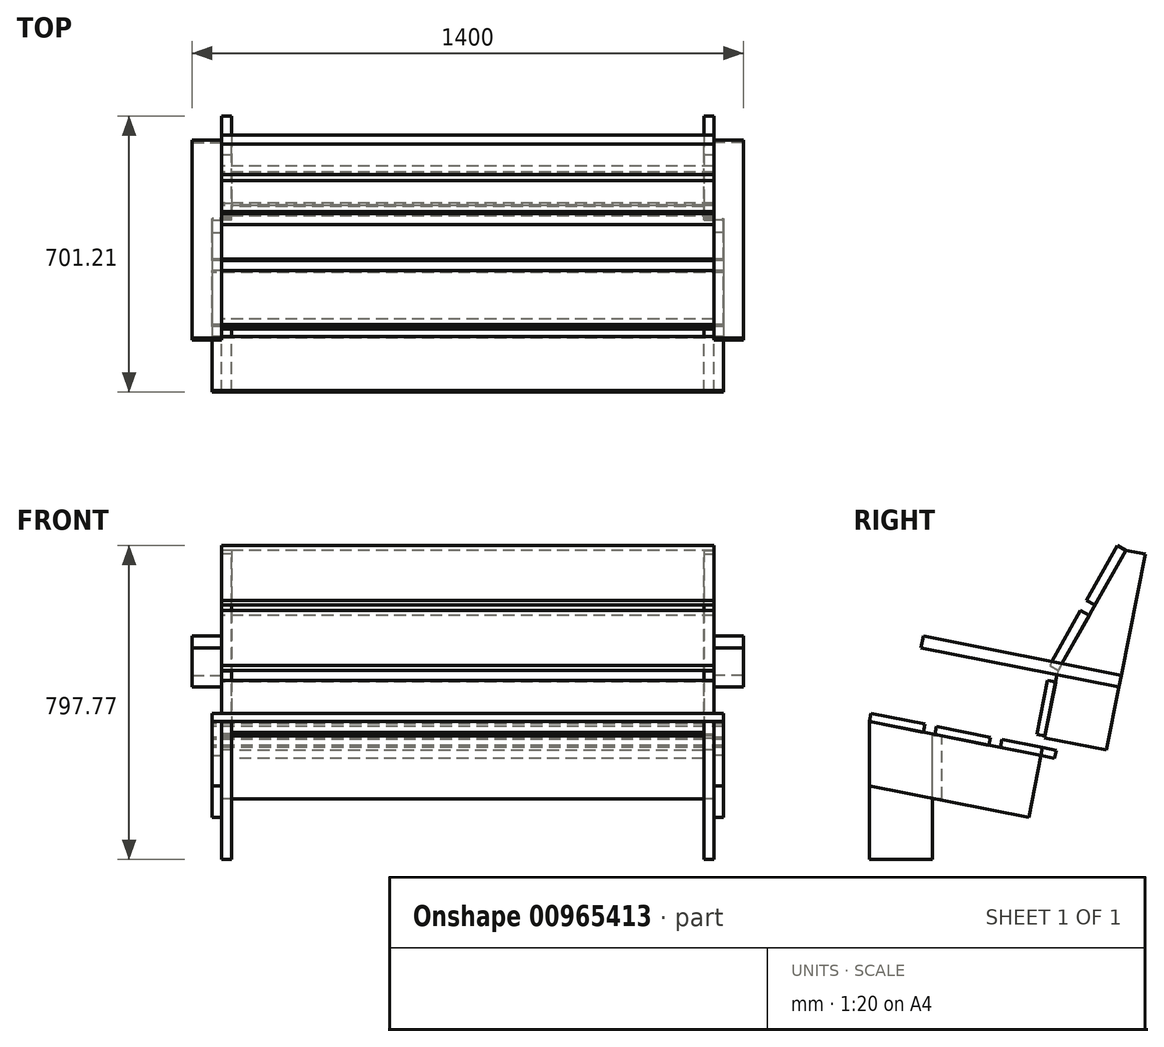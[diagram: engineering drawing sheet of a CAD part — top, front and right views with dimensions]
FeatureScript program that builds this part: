
annotation { "Feature Type Name" : "Feature", "Feature Type Description" : "" }
export const myFeature = defineFeature(function(context is Context, id is Id, definition is map)
    precondition{}
    {
        {
            var Q0;
            Q0=qCreatedBy(makeId("Right.planeOp"),FACE);
            var sketch = newSketch(context, id + "F0", { "sketchPlane" : qUnion([Q0])});
            skPoint(sketch, "E0", {"position": v(-249.54, -686.48) * mm});
            skPoint(sketch, "E1", {"position": v(-237.44, -315.62) * mm});
            skLineSegment(sketch, "E2", {"start": v(-249.54, -686.48) * mm, "end": v(295.32, -698.73) * mm});
            skLineSegment(sketch, "E3", {"start": v(-249.54, -686.48) * mm, "end": v(-249.54, -335.98) * mm});
            skLineSegment(sketch, "E4", {"start": v(295.32, -698.73) * mm, "end": v(451.67, 89.28) * mm});
            skLineSegment(sketch, "E5", {"start": v(451.67, 89.28) * mm, "end": v(402.62, 99) * mm});
            skLineSegment(sketch, "E6", {"start": v(343.93, -453.73) * mm, "end": v(-249.54, -335.98) * mm});
            skLineSegment(sketch, "E7", {"start": v(312.8, -610.67) * mm, "end": v(-249.54, -499.1) * mm});
            skLineSegment(sketch, "E8", {"start": v(229.62, -207.76) * mm, "end": v(132.92, -695.08) * mm});
            skLineSegment(sketch, "E9", {"start": v(-89.54, -690.08) * mm, "end": v(-89.54, -367.73) * mm});
            skLineSegment(sketch, "E10", {"start": v(402.62, 99) * mm, "end": v(229.62, -207.76) * mm});
            skLineSegment(sketch, "E11", {"start": v(390.56, -218.73) * mm, "end": v(-112.01, -119.02) * mm});
            skLineSegment(sketch, "E12", {"start": v(-112.01, -119.02) * mm, "end": v(-117.85, -148.44) * mm});
            skLineSegment(sketch, "E13", {"start": v(-117.85, -148.44) * mm, "end": v(384.72, -248.16) * mm});
            skLineSegment(sketch, "E14", {"start": v(-87.74, -342.6) * mm, "end": v(-92.6, -367.12) * mm});
            skLineSegment(sketch, "E15", {"start": v(-87.74, -342.6) * mm, "end": v(-244.68, -311.46) * mm});
            skLineSegment(sketch, "E16", {"start": v(-249.54, -335.98) * mm, "end": v(-244.68, -311.46) * mm});
            skPoint(sketch, "E17", {"position": v(-43.69, -350.7) * mm});
            skPoint(sketch, "E18", {"position": v(-13.73, -354.7) * mm});
            skLineSegment(sketch, "E19.0", {"start": v(-58.31, -348.44) * mm, "end": v(-63.18, -372.96) * mm});
            skLineSegment(sketch, "E20", {"start": v(-58.31, -348.44) * mm, "end": v(98.63, -379.57) * mm});
            skLineSegment(sketch, "E21", {"start": v(98.63, -379.57) * mm, "end": v(93.76, -404.1) * mm});
            skLineSegment(sketch, "E22.0", {"start": v(128.06, -385.41) * mm, "end": v(123.2, -409.94) * mm});
            skLineSegment(sketch, "E23", {"start": v(128.06, -385.41) * mm, "end": v(285, -416.55) * mm});
            skLineSegment(sketch, "E24", {"start": v(285, -416.55) * mm, "end": v(280.13, -441.07) * mm});
            skLineSegment(sketch, "E25.0", {"start": v(-64.54, -690.08) * mm, "end": v(-64.54, -367.73) * mm});
            skLineSegment(sketch, "E26", {"start": v(402.62, 99) * mm, "end": v(380.85, 111.29) * mm});
            skLineSegment(sketch, "E27", {"start": v(380.85, 111.29) * mm, "end": v(302.25, -28.08) * mm});
            skLineSegment(sketch, "E28", {"start": v(302.25, -28.08) * mm, "end": v(324.03, -40.36) * mm});
            skLineSegment(sketch, "E29.0", {"start": v(287.51, -54.2) * mm, "end": v(309.29, -66.49) * mm});
            skLineSegment(sketch, "E30", {"start": v(287.51, -54.2) * mm, "end": v(208.91, -193.57) * mm});
            skLineSegment(sketch, "E31", {"start": v(208.91, -193.57) * mm, "end": v(230.69, -205.85) * mm});
            skPoint(sketch, "E32.orphan", {"position": v(229.62, -205.25) * mm});
            skLineSegment(sketch, "E33", {"start": v(229.62, -207.76) * mm, "end": v(205.1, -202.89) * mm});
            skLineSegment(sketch, "E34", {"start": v(205.1, -202.89) * mm, "end": v(173.95, -359.83) * mm});
            skLineSegment(sketch, "E35", {"start": v(173.95, -359.83) * mm, "end": v(198.48, -364.7) * mm});
            skSolve(sketch);
        }
        {
            var Q0;
            Q0=qCreatedBy(makeId("Right.planeOp"),FACE);
            var sketch = newSketch(context, id + "F1", { "sketchPlane" : qUnion([Q0])});
            skLineSegment(sketch, "E36.bottom", {"start": v(-245.46, -315.38) * mm, "end": v(-108.13, -342.63) * mm});
            skLineSegment(sketch, "E36.top", {"start": v(-249.54, -335.98) * mm, "end": v(-112.22, -363.23) * mm});
            skLineSegment(sketch, "E36.left", {"start": v(-249.54, -335.98) * mm, "end": v(-245.46, -315.38) * mm});
            skLineSegment(sketch, "E36.right", {"start": v(-112.22, -363.23) * mm, "end": v(-108.13, -342.63) * mm});
            skSolve(sketch);
        }
        {
            var Q0;
            Q0 = qSketchRegion(id + "F1", true);
            extrude(context, id + "F2", {"entities" : qUnion([Q0]), "depth" : 1300 * mm, "offsetDistance" : 25 * mm});
        }
        {
            var Q0;
            Q0=qCreatedBy(makeId("Right.planeOp"),FACE);
            var sketch = newSketch(context, id + "F3", { "sketchPlane" : qUnion([Q0])});
            skLineSegment(sketch, "E37", {"start": v(-82.8, -369.07) * mm, "end": v(54.53, -396.31) * mm});
            skLineSegment(sketch, "E38", {"start": v(-82.8, -369.07) * mm, "end": v(-78.7, -348.47) * mm});
            skLineSegment(sketch, "E39", {"start": v(-78.7, -348.47) * mm, "end": v(58.62, -375.71) * mm});
            skLineSegment(sketch, "E40", {"start": v(54.53, -396.31) * mm, "end": v(58.62, -375.71) * mm});
            skSolve(sketch);
        }
        {
            var Q0;
            Q0 = qSketchRegion(id + "F3", true);
            extrude(context, id + "F4", {"entities" : qUnion([Q0]), "depth" : 1300 * mm, "offsetDistance" : 25 * mm});
        }
        {
            var Q0;
            Q0=qCreatedBy(makeId("Right.planeOp"),FACE);
            var sketch = newSketch(context, id + "F5", { "sketchPlane" : qUnion([Q0])});
            skLineSegment(sketch, "E41.0", {"start": v(88.04, -381.55) * mm, "end": v(83.96, -402.15) * mm});
            skLineSegment(sketch, "E42.0", {"start": v(225.37, -408.8) * mm, "end": v(221.28, -429.4) * mm});
            skLineSegment(sketch, "E43", {"start": v(83.96, -402.15) * mm, "end": v(221.28, -429.4) * mm});
            skLineSegment(sketch, "E44", {"start": v(88.04, -381.55) * mm, "end": v(225.37, -408.8) * mm});
            skSolve(sketch);
        }
        {
            var Q0;
            Q0 = qSketchRegion(id + "F5", true);
            extrude(context, id + "F6", {"entities" : qUnion([Q0]), "depth" : 1300 * mm, "offsetDistance" : 25 * mm});
        }
        {
            var Q0;
            Q0=qCreatedBy(makeId("Right.planeOp"),FACE);
            var sketch = newSketch(context, id + "F7", { "sketchPlane" : qUnion([Q0])});
            skLineSegment(sketch, "E45", {"start": v(224.16, -235.25) * mm, "end": v(196.91, -372.57) * mm});
            skLineSegment(sketch, "E46.0", {"start": v(224.16, -235.25) * mm, "end": v(203.56, -231.16) * mm});
            skLineSegment(sketch, "E47.0", {"start": v(176.32, -368.48) * mm, "end": v(196.91, -372.57) * mm});
            skPoint(sketch, "E48.orphan", {"position": v(205.1, -202.89) * mm});
            skLineSegment(sketch, "E49", {"start": v(203.56, -231.16) * mm, "end": v(176.32, -368.48) * mm});
            skSolve(sketch);
        }
        {
            var Q0;
            Q0 = qSketchRegion(id + "F7", true);
            extrude(context, id + "F8", {"entities" : qUnion([Q0]), "depth" : (1300 - 25) * mm, "offsetDistance" : 25 * mm, "hasSecondDirection" : true, "secondDirectionOppositeDirection" : false, "secondDirectionDepth" : 25 * mm});
        }
        {
            var Q0;
            {var subQ0=sQuery(id+"F0.wireOp",EDGE,"E29.0");Q0=makeQuery(id+"F0.imprint","IMPRINT",FACE,{"disambiguationData":[TD([[makeQuery(id+"F0.imprint","IMPRINT",EDGE,{"derivedFrom":subQ0}),-1.0]])]});}
            var Q1;
            {var subQ0=sQuery(id+"F0.wireOp",EDGE,"E31");Q1=makeQuery(id+"F0.imprint","IMPRINT",FACE,{"disambiguationData":[TD([[makeQuery(id+"F0.imprint","IMPRINT",EDGE,{"derivedFrom":subQ0}),1.0]])]});}
            extrude(context, id + "F9", {"entities" : qUnion([Q0, Q1]), "depth" : (1300 - 25) * mm, "offsetDistance" : 25 * mm, "hasSecondDirection" : true, "secondDirectionOppositeDirection" : false, "secondDirectionDepth" : 25 * mm});
        }
        {
            var Q0;
            {var subQ0=sQuery(id+"F0.wireOp",EDGE,"E26");Q0=makeQuery(id+"F0.imprint","IMPRINT",FACE,{"disambiguationData":[TD([[makeQuery(id+"F0.imprint","IMPRINT",EDGE,{"derivedFrom":subQ0}),1.0]])]});}
            extrude(context, id + "F10", {"entities" : qUnion([Q0]), "depth" : (1300 - 25) * mm, "offsetDistance" : 25 * mm, "hasSecondDirection" : true, "secondDirectionOppositeDirection" : false, "secondDirectionDepth" : 25 * mm});
        }
        {
            var Q0;
            Q0=qCreatedBy(makeId("Right.planeOp"),FACE);
            var sketch = newSketch(context, id + "F11", { "sketchPlane" : qUnion([Q0])});
            skLineSegment(sketch, "E50.0", {"start": v(312.8, -610.67) * mm, "end": v(-249.54, -499.1) * mm});
            skLineSegment(sketch, "E51.0", {"start": v(343.93, -453.73) * mm, "end": v(-249.54, -335.98) * mm});
            skLineSegment(sketch, "E52", {"start": v(343.93, -453.73) * mm, "end": v(312.8, -610.67) * mm});
            skLineSegment(sketch, "E53", {"start": v(-249.54, -335.98) * mm, "end": v(-249.54, -499.1) * mm});
            skSolve(sketch);
        }
        {
            var Q0;
            Q0 = qSketchRegion(id + "F11", true);
            extrude(context, id + "F12", {"entities" : qUnion([Q0]), "depth" : 25 * mm, "offsetDistance" : 25 * mm});
        }
        {
            var Q0;
            Q0=qCreatedBy(makeId("Right.planeOp"),FACE);
            var sketch = newSketch(context, id + "F13", { "sketchPlane" : qUnion([Q0])});
            skLineSegment(sketch, "E54.0", {"start": v(390.56, -218.73) * mm, "end": v(-112.01, -119.02) * mm});
            skLineSegment(sketch, "E55.0", {"start": v(-117.85, -148.44) * mm, "end": v(384.72, -248.16) * mm});
            skLineSegment(sketch, "E56.0", {"start": v(-112.01, -119.02) * mm, "end": v(-117.85, -148.44) * mm});
            skLineSegment(sketch, "E57", {"start": v(390.56, -218.73) * mm, "end": v(384.72, -248.16) * mm});
            skSolve(sketch);
        }
        {
            var Q0;
            Q0 = qSketchRegion(id + "F13", true);
            extrude(context, id + "F14", {"entities" : qUnion([Q0]), "oppositeDirection" : true, "depth" : 50 * mm, "offsetDistance" : 25 * mm, "hasSecondDirection" : true, "secondDirectionOppositeDirection" : false, "secondDirectionDepth" : 25 * mm});
        }
        {
            var Q0;
            Q0=qCreatedBy(makeId("Right.planeOp"),FACE);
            var sketch = newSketch(context, id + "F15", { "sketchPlane" : qUnion([Q0])});
            skLineSegment(sketch, "E58.0", {"start": v(-249.54, -686.48) * mm, "end": v(-249.54, -335.98) * mm});
            skLineSegment(sketch, "E59.0", {"start": v(-89.54, -686.48) * mm, "end": v(-89.54, -367.73) * mm});
            skLineSegment(sketch, "E60", {"start": v(-249.54, -335.98) * mm, "end": v(-89.54, -367.73) * mm});
            skLineSegment(sketch, "E61", {"start": v(-249.54, -686.48) * mm, "end": v(-89.54, -686.48) * mm});
            skPoint(sketch, "E62.orphan", {"position": v(-89.54, -690.08) * mm});
            skSolve(sketch);
        }
        {
            var Q0;
            Q0 = qSketchRegion(id + "F15", true);
            extrude(context, id + "F16", {"entities" : qUnion([Q0]), "depth" : 50 * mm, "offsetDistance" : 25 * mm, "hasSecondDirection" : true, "secondDirectionOppositeDirection" : true, "secondDirectionDepth" : -25 * mm});
        }
        {
            var Q0;
            Q0=qCreatedBy(makeId("Right.planeOp"),FACE);
            var sketch = newSketch(context, id + "F17", { "sketchPlane" : qUnion([Q0])});
            skLineSegment(sketch, "E63.0", {"start": v(297.75, -686.48) * mm, "end": v(451.67, 89.28) * mm});
            skLineSegment(sketch, "E64.0", {"start": v(229.62, -207.76) * mm, "end": v(134.63, -686.48) * mm});
            skLineSegment(sketch, "E65.0", {"start": v(402.62, 99) * mm, "end": v(229.62, -207.76) * mm});
            skLineSegment(sketch, "E66", {"start": v(402.62, 99) * mm, "end": v(451.67, 89.28) * mm});
            skPoint(sketch, "E67.0", {"position": v(-249.54, -686.48) * mm});
            skLineSegment(sketch, "E68", {"start": v(134.63, -686.48) * mm, "end": v(297.75, -686.48) * mm});
            skSolve(sketch);
        }
        {
            var Q0;
            Q0 = qSketchRegion(id + "F17", true);
            extrude(context, id + "F18", {"entities" : qUnion([Q0]), "depth" : 50 * mm, "offsetDistance" : 25 * mm, "hasSecondDirection" : true, "secondDirectionOppositeDirection" : true, "secondDirectionDepth" : -25 * mm});
        }
        {
            var Q0;
            Q0=qCreatedBy(makeId("Right.planeOp"),FACE);
            var sketch = newSketch(context, id + "F19", { "sketchPlane" : qUnion([Q0])});
            skLineSegment(sketch, "E69.0", {"start": v(-64.54, -532.42) * mm, "end": v(-64.54, -372.42) * mm});
            skLineSegment(sketch, "E70.0", {"start": v(-89.54, -532.42) * mm, "end": v(-89.54, -372.42) * mm});
            skPoint(sketch, "E71.0", {"position": v(-249.54, -511.23) * mm});
            skLineSegment(sketch, "E72", {"start": v(-64.54, -372.42) * mm, "end": v(-89.54, -372.42) * mm});
            skLineSegment(sketch, "E73.0", {"start": v(-64.54, -532.42) * mm, "end": v(-89.54, -532.42) * mm});
            skPoint(sketch, "E74.orphan", {"position": v(-64.54, -690.08) * mm});
            skPoint(sketch, "E75.orphan", {"position": v(-89.54, -690.08) * mm});
            skPoint(sketch, "E76.orphan", {"position": v(-89.54, -367.73) * mm});
            skPoint(sketch, "E77.orphan", {"position": v(-64.54, -367.73) * mm});
            skSolve(sketch);
        }
        {
            var Q0;
            Q0 = qSketchRegion(id + "F19", true);
            extrude(context, id + "F20", {"entities" : qUnion([Q0]), "depth" : (1300 - 25) * mm, "offsetDistance" : 25 * mm, "hasSecondDirection" : true, "secondDirectionOppositeDirection" : false, "secondDirectionDepth" : 25 * mm});
        }
        {
            var Q0;
            Q0=qCreatedBy(makeId("Right.planeOp"),FACE);
            cPlane(context, id + "F21", {"entities" : qUnion([Q0]), "cplaneType" : CPlaneType.OFFSET, "offset" : (1300 / 2) * mm, "width" : 150 * mm, "height" : 150 * mm});
        }
        {
            var Q0;
            Q0=makeQuery(id+"F18.opExtrude","SWEPT_BODY",BODY,{"disambiguationData":[OSD([sQuery(id+"F17.wireOp",EDGE,"E63.0"),sQuery(id+"F17.wireOp",EDGE,"E64.0"),sQuery(id+"F17.wireOp",EDGE,"E65.0"),sQuery(id+"F17.wireOp",EDGE,"E66"),sQuery(id+"F17.wireOp",EDGE,"yx6k0d1h-Bgtg-5VNX-LB6u-sacaECDwNLv2")])]});
            var Q1;
            Q1=makeQuery(id+"F16.opExtrude","SWEPT_BODY",BODY,{"disambiguationData":[OSD([sQuery(id+"F15.wireOp",EDGE,"E58.0"),sQuery(id+"F15.wireOp",EDGE,"E59.0"),sQuery(id+"F15.wireOp",EDGE,"ApE2fH3A-TVtd-ZWUS-5VCc-9abMuy0xFYwQ"),sQuery(id+"F15.wireOp",EDGE,"E60")])]});
            var Q2;
            Q2=makeQuery(id+"F12.opExtrude","SWEPT_BODY",BODY,{"disambiguationData":[OSD([sQuery(id+"F11.wireOp",EDGE,"E50.0"),sQuery(id+"F11.wireOp",EDGE,"E51.0"),sQuery(id+"F11.wireOp",EDGE,"E52"),sQuery(id+"F11.wireOp",EDGE,"E53")])]});
            var Q3;
            Q3=makeQuery(id+"F14.opExtrude","SWEPT_BODY",BODY,{"disambiguationData":[OSD([sQuery(id+"F13.wireOp",EDGE,"E54.0"),sQuery(id+"F13.wireOp",EDGE,"E55.0"),sQuery(id+"F13.wireOp",EDGE,"E56.0"),sQuery(id+"F13.wireOp",EDGE,"E57")])]});
            var Q4;
            Q4=qCreatedBy(id+"F21.planeOp",FACE);
            mirror(context, id + "F22", {"entities" : qUnion([Q0, Q1, Q2, Q3]), "mirrorPlane" : qUnion([Q4])});
        }
        {
            var Q0;
            Q0=makeQuery(id+"F2.opExtrude","SWEPT_FACE",FACE,{"disambiguationData":[OSD([sQuery(id+"F1.wireOp",EDGE,"E36.bottom")])]});
            cPlane(context, id + "F23", {"entities" : qUnion([Q0]), "cplaneType" : CPlaneType.OFFSET, "offset" : 25 * mm, "width" : 150 * mm, "height" : 150 * mm});
        }
        {
            var Q0;
            Q0=qCreatedBy(id+"F23.planeOp",FACE);
            var sketch = newSketch(context, id + "F24", { "sketchPlane" : qUnion([Q0])});
            skPoint(sketch, "E78.0", {"position": v(50, 265.66) * mm});
            skLineSegment(sketch, "E79.bottom", {"start": v(50, 265.66) * mm, "end": v(-39.83, 265.66) * mm});
            skLineSegment(sketch, "E79.top", {"start": v(50, 450.15) * mm, "end": v(-39.83, 450.15) * mm});
            skLineSegment(sketch, "E79.left", {"start": v(50, 265.66) * mm, "end": v(50, 450.15) * mm});
            skLineSegment(sketch, "E79.right", {"start": v(-39.83, 265.66) * mm, "end": v(-39.83, 450.15) * mm});
            skPoint(sketch, "E80.0", {"position": v(1250, 265.66) * mm});
            skLineSegment(sketch, "E81.bottom", {"start": v(1250, 265.66) * mm, "end": v(1386.33, 265.66) * mm});
            skLineSegment(sketch, "E81.top", {"start": v(1250, 490.16) * mm, "end": v(1386.33, 490.16) * mm});
            skLineSegment(sketch, "E81.left", {"start": v(1250, 265.66) * mm, "end": v(1250, 490.16) * mm});
            skLineSegment(sketch, "E81.right", {"start": v(1386.33, 265.66) * mm, "end": v(1386.33, 490.16) * mm});
            skSolve(sketch);
        }
        {
            var Q0;
            Q0 = qSketchRegion(id + "F24", true);
            extrude(context, id + "F25", {"entities" : qUnion([Q0]), "operationType" : NewBodyOperationType.REMOVE, "endBound" : BoundingType.THROUGH_ALL, "oppositeDirection" : true, "depth" : 25 * mm, "offsetDistance" : 25 * mm});
        }
    });
